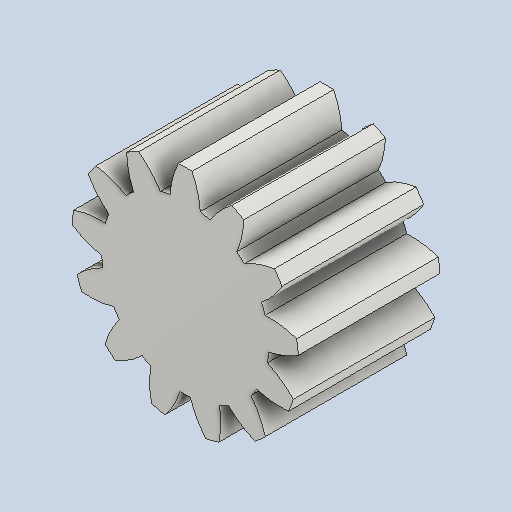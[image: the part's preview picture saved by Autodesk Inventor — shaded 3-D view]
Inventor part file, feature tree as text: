
AUTODESK INVENTOR PART (.ipt)
format: ipt  version: 2023.1 (Build 271208000, 208)  size: 224,256 bytes
history: native  units: mm (DEFAULTED — no unit token found)
features: plane x3, other x3, sketch x2, extrude x1
ambient origin geometry x8: Origin, YZ Plane, XZ Plane, XY Plane, X Axis, Y Axis, Z Axis, Center Point
bodies: Solid1 (feature_tree)
feature tree (9):
  extrude  "Extrusion1"  Depth=20.0mm TaperAngle=0.0deg
  plane  "Work Plane2"
  plane  "Work Plane8"
  plane  "Work Plane9"
  other  "Spur Gear"
  sketch  "Sketch1"  dims[d0=32.0mm d1=20.0mm d2=0.0mm]
  sketch  "Sketch2"  dims[d3=26.0mm d4=10.0mm d5=0.0mm d16=20.0mm d17=0.0mm d34=2.41661mm d39=0.0mm d41=0.0mm d43=20.0mm d46=20.0mm d47=0.0mm d48=0.0mm]
  other  "Srf1"
  other  "Pitch Diameter"
